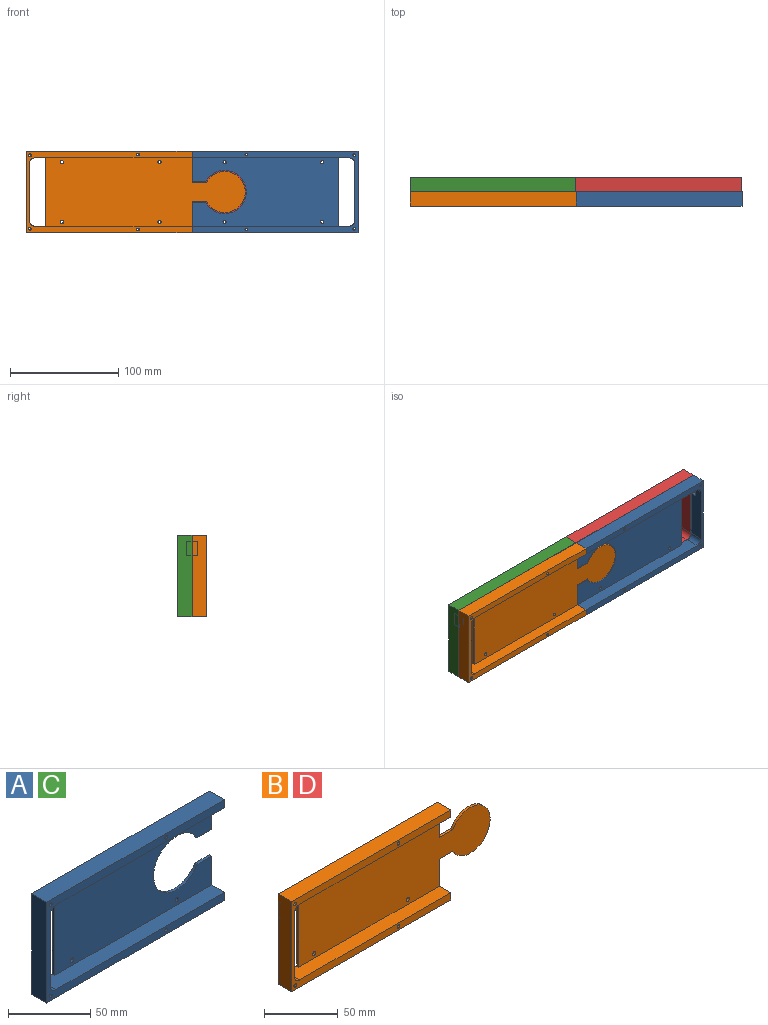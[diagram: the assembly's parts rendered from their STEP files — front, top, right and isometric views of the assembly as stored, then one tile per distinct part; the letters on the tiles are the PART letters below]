
ASSEMBLY  parts=4 mates=3
PART A: 28 faces, bbox 153x13x75 mm
  f0: plane 53x13mm, normal (1,0,0), area 645mm2, adj f1,f9,f19,f20,f22,f23
  f1: plane 153x75mm, normal (0,1,0), area 8981mm2, adj f0,f2,f3,f4,f5,f6,f7,f8
  f2: plane 75x13mm, normal (-1,0,0), area 975mm2, adj f1,f3,f8,f9
  f3: plane 153x13mm, normal (0,0,-1), area 1989mm2, adj f1,f2,f4,f9
  f4: plane 27.5x13mm, normal (1,0,0), area 121mm2, adj f1,f3,f5,f9,f12,f13
  f5: plane 152.5x13mm, normal (0,0,1), area 1656.2mm2, adj f1,f4,f9,f13,f14,f20,f21,f22
  f6: plane 145x13mm, normal (0,0,-1), area 1615mm2, adj f1,f7,f9,f13,f14,f23
  f7: plane 27.5x13mm, normal (1,0,0), area 121mm2, adj f1,f6,f8,f9,f10,f13
  f8: plane 153x13mm, normal (0,0,1), area 1989mm2, adj f1,f2,f7,f9
  f9: plane 153x75mm, normal (0,-1,0), area 2016.1mm2, adj f0,f2,f3,f4,f5,f6,f7,f8
  f10: plane 12.68x2mm, normal (0,0,-1), area 25.4mm2, adj f1,f7,f11,f13
  f11: cylinder r=20mm len=40mm, axis (0,1,0), area 209.4mm2, adj f1,f10,f12,f13
  f12: plane 12.68x2mm, normal (0,0,1), area 25.4mm2, adj f1,f4,f11,f13
  f13: plane 135x63mm, normal (0,-1,0), area 7002.7mm2, adj f4,f5,f6,f7,f10,f11,f12,f14
  f14: plane 63x2mm, normal (-1,0,0), area 126mm2, adj f1,f5,f6,f13
  f15: cylinder r=1.5mm len=3mm, axis (0,-1,0), area 18.8mm2, adj f1,f13
  f16: cylinder r=1.5mm len=3mm, axis (0,-1,0), area 18.8mm2, adj f1,f13
  f17: cylinder r=1.5mm len=3mm, axis (0,-1,0), area 18.8mm2, adj f1,f13
  f18: cylinder r=1.5mm len=3mm, axis (0,-1,0), area 18.8mm2, adj f1,f13
  f19: plane 5.5x2.5mm, normal (0,0,-1), area 13.7mm2, adj f0,f1,f20,f21
  f20: plane 13x7.5mm, normal (0,1,0), area 37.9mm2, adj f0,f5,f19,f21,f22
  f21: plane 13x5.5mm, normal (1,0,0), area 71.5mm2, adj f1,f5,f19,f20
  f22: cylinder r=5mm len=7.5mm, axis (0,-1,0), area 58.9mm2, adj f0,f5,f9,f20
  f23: cylinder r=5mm len=13mm, axis (0,-1,0), area 102.1mm2, adj f0,f1,f6,f9
  f24: cylinder r=1.25mm len=13mm, axis (0,-1,0), area 102.1mm2, adj f1,f9
  f25: cylinder r=1.25mm len=13mm, axis (0,-1,0), area 102.1mm2, adj f1,f9
  f26: cylinder r=1.25mm len=13mm, axis (0,-1,0), area 102.1mm2, adj f1,f9
  f27: cylinder r=1.25mm len=13mm, axis (0,-1,0), area 102.1mm2, adj f1,f9
PART B: 28 faces, bbox 202x13x75 mm
  f0: plane 202x75mm, normal (0,1,0), area 11800.3mm2, adj f1,f2,f3,f4,f5,f6,f7,f8
  f1: plane 75x13mm, normal (-1,0,0), area 975mm2, adj f0,f2,f8,f9
  f2: plane 153x13mm, normal (0,0,-1), area 1989mm2, adj f0,f1,f3,f9
  f3: plane 28.5x13mm, normal (1,0,0), area 123mm2, adj f0,f2,f4,f9,f12,f13
  f4: plane 145x13mm, normal (0,0,1), area 1615mm2, adj f0,f3,f9,f13,f14,f22
  f5: plane 53x13mm, normal (1,0,0), area 645mm2, adj f0,f9,f19,f20,f22,f23
  f6: plane 152.5x13mm, normal (0,0,-1), area 1656.2mm2, adj f0,f7,f9,f13,f14,f20,f21,f23
  f7: plane 28.5x13mm, normal (1,0,0), area 123mm2, adj f0,f6,f8,f9,f10,f13
  f8: plane 153x13mm, normal (0,0,1), area 1989mm2, adj f0,f1,f7,f9
  f9: plane 153x75mm, normal (0,-1,0), area 2016.1mm2, adj f1,f2,f3,f4,f5,f6,f7,f8
  f10: plane 13.27x2mm, normal (0,0,1), area 26.5mm2, adj f0,f7,f11,f13
  f11: cylinder r=19mm len=38mm, axis (0,1,0), area 201.3mm2, adj f0,f10,f12,f13
  f12: plane 13.27x2mm, normal (0,0,-1), area 26.5mm2, adj f0,f3,f11,f13
  f13: plane 184x63mm, normal (0,-1,0), area 9822.1mm2, adj f3,f4,f6,f7,f10,f11,f12,f14
  f14: plane 63x2mm, normal (-1,0,0), area 126mm2, adj f0,f4,f6,f13
  f15: cylinder r=1.5mm len=3mm, axis (0,-1,0), area 18.8mm2, adj f0,f13
  f16: cylinder r=1.5mm len=3mm, axis (0,-1,0), area 18.8mm2, adj f0,f13
  f17: cylinder r=1.5mm len=3mm, axis (0,-1,0), area 18.8mm2, adj f0,f13
  f18: cylinder r=1.5mm len=3mm, axis (0,-1,0), area 18.8mm2, adj f0,f13
  f19: plane 5.5x2.5mm, normal (0,0,1), area 13.7mm2, adj f0,f5,f20,f21
  f20: plane 13x7.5mm, normal (0,1,0), area 37.9mm2, adj f5,f6,f19,f21,f23
  f21: plane 13x5.5mm, normal (1,0,0), area 71.5mm2, adj f0,f6,f19,f20
  f22: cylinder r=5mm len=13mm, axis (0,-1,0), area 102.1mm2, adj f0,f4,f5,f9
  f23: cylinder r=5mm len=7.5mm, axis (0,-1,0), area 58.9mm2, adj f5,f6,f9,f20
  f24: cylinder r=1.25mm len=13mm, axis (0,-1,0), area 102.1mm2, adj f0,f9
  f25: cylinder r=1.25mm len=13mm, axis (0,-1,0), area 102.1mm2, adj f0,f9
  f26: cylinder r=1.25mm len=13mm, axis (0,-1,0), area 102.1mm2, adj f0,f9
  f27: cylinder r=1.25mm len=13mm, axis (0,-1,0), area 102.1mm2, adj f0,f9
PART C: same geometry as A
PART D: same geometry as B
PLACE A rot(axis=(0,1,0),180deg) t=(364.54,22,200.39)mm
PLACE B t=(58.54,22,125.39)mm
PLACE C rot(axis=(1,0,0),180deg) t=(58.37,22,200.44)mm
PLACE D rot(axis=(0,0,1),180deg) t=(364.37,22,125.44)mm
MATE fastened D.f11 <-> C.f11  axis (0,1,0) through (181.37,24,162.94)mm
MATE planar C.f1 <-> B.f0  axis (0,-1,0) through (133.87,22,162.83)mm
MATE fastened A.f11 <-> B.f11  axis (0,-1,0) through (241.54,20,162.89)mm
